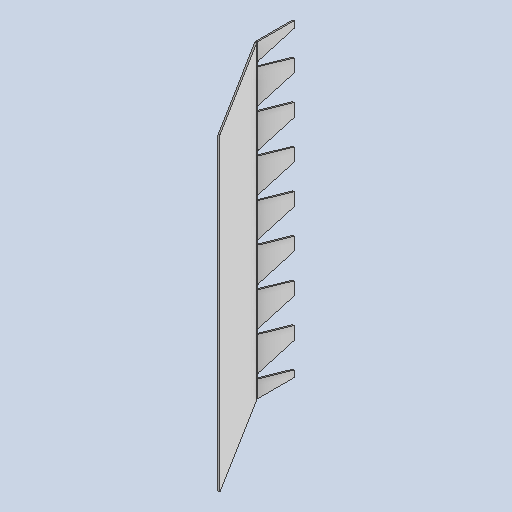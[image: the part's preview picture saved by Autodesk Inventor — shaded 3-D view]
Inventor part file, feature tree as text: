
AUTODESK INVENTOR PART (.ipt)
format: ipt  version: 2025 (Build 290162010, 162A)  size: 360,960 bytes
history: native  units: mm
features: sheet_metal_op x3, other x3, sketch x2, extrude x1, pattern_linear x1, projected_geometry x1
ambient origin geometry x8: Origin, YZ Plane, XZ Plane, XY Plane, X Axis, Y Axis, Z Axis, Center Point
bodies: Solid1 (feature_tree)
feature tree (11):
  sheet_metal_op  "Contour Flange1"
  other  "A-Side Definition"
  extrude  "Extrusion1"  Depth=5.585054mm
  pattern_linear  "Rectangular Pattern1"  Spacing1=1.0mm  [1 undecoded]
  sketch  "Sketch1"  dims[d0=950.73mm d2=5.585054mm]
  other  "Plate1"
  sheet_metal_op  "Bend1"
  sheet_metal_op  "Corner1"
  sketch  "Sketch2"  dims[d3=814.155775mm d4=1.0mm d5=10.0mm d6=10.0mm d7=5.0mm d8=20.0mm d9=10.0mm d10=2161.0mm d11=10.0mm d12=10.0mm d13=40.0mm d14=10.0mm d15=10.0mm d16=260.0mm d17=20.0mm d18=5.585054mm d19=46.0mm d20=0.0mm d21=0.0mm d22=80.0mm d24=270.0mm]
  projected_geometry  "Projected Loop1"
  other  "Definition1"
note: 1 required parameter value undecoded (feature->parameter linkage not recoverable at this tier; creation-order binding heuristic only, values carry confidence <= 0.55)
